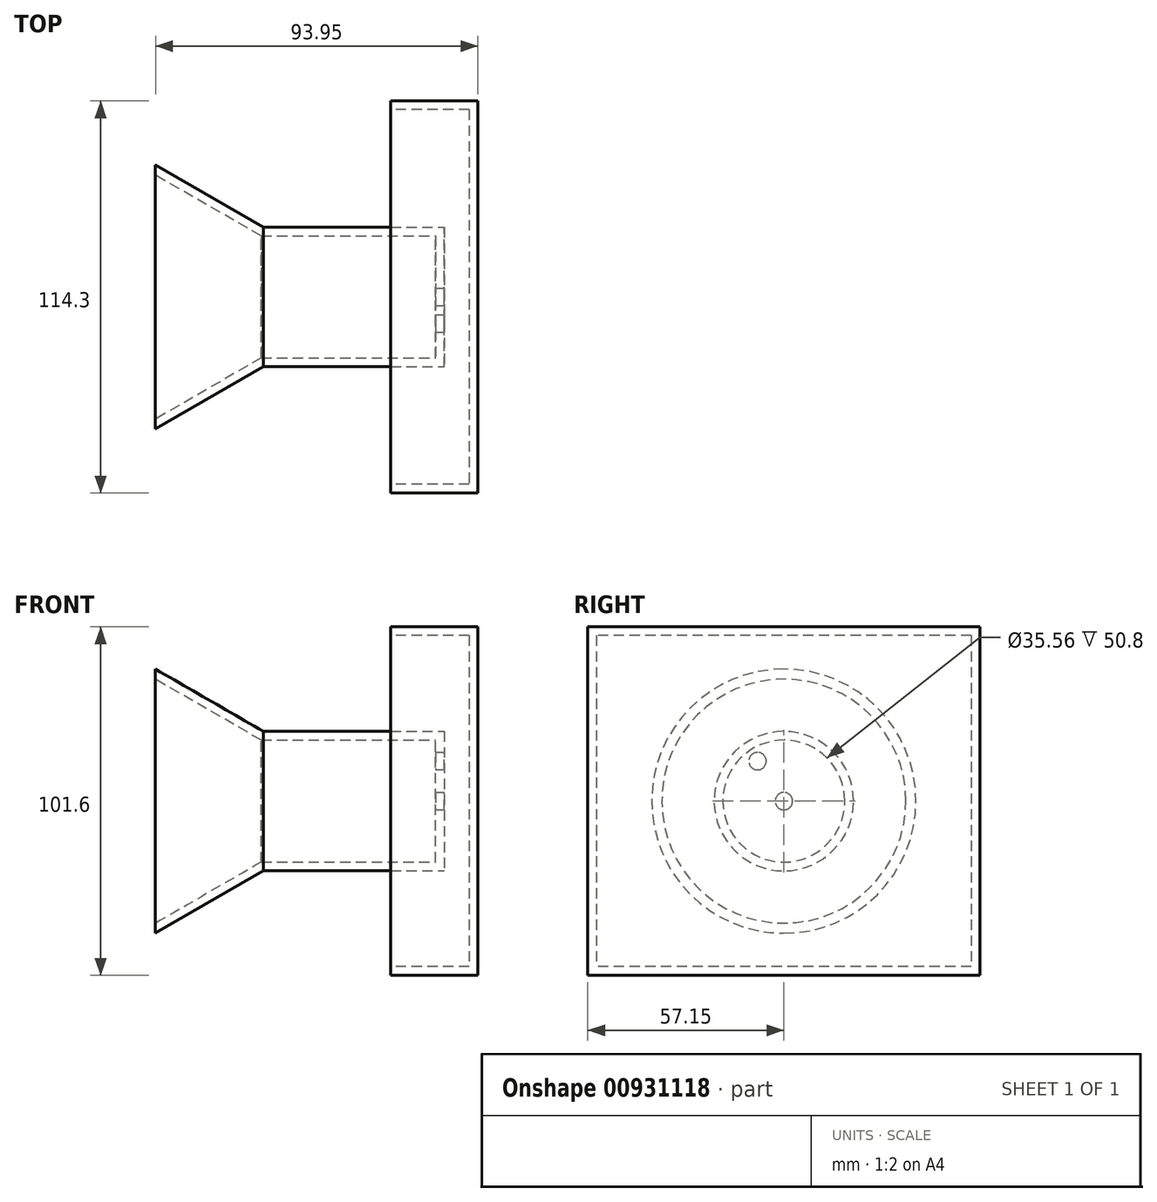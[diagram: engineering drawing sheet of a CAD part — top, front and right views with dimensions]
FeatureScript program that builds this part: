
annotation { "Feature Type Name" : "Feature", "Feature Type Description" : "" }
export const myFeature = defineFeature(function(context is Context, id is Id, definition is map)
    precondition{}
    {
        {
            var Q0;
            Q0=qCreatedBy(makeId("Front.planeOp"),FACE);
            var sketch = newSketch(context, id + "F0", { "sketchPlane" : qUnion([Q0])});
            skLineSegment(sketch, "E0", {"start": v(-55.85, 35.56) * mm, "end": v(-25.06, 17.78) * mm});
            skLineSegment(sketch, "E1", {"start": v(-25.06, 17.78) * mm, "end": v(25.74, 17.78) * mm});
            skLineSegment(sketch, "E2", {"start": v(25.74, 17.78) * mm, "end": v(25.74, 0) * mm});
            skLineSegment(sketch, "E3", {"start": v(25.74, 0) * mm, "end": v(-55.85, 0) * mm});
            skLineSegment(sketch, "E4", {"start": v(-55.85, 0) * mm, "end": v(-55.85, 35.56) * mm});
            skSolve(sketch);
        }
        {
            var Q0;
            Q0=makeQuery(id+"F0.imprint","IMPRINT",FACE,{"disambiguationData":[TD([[makeQuery(id+"F0.imprint","IMPRINT",EDGE,{"derivedFrom":sQuery(id+"F0.wireOp",EDGE,"E0")}),-1.0]])]});
            var Q1;
            Q1=sQuery(id+"F0.wireOp",EDGE,"E3");
            revolve(context, id + "F1", {"surfaceOperationType" : NewSurfaceOperationType.NEW, "entities" : qUnion([Q0]), "axis" : qUnion([Q1]), "revolveType" : RevolveType.FULL});
        }
        {
            var Q0;
            Q0=makeQuery(id+"F1.opRevolve","SWEPT_FACE",FACE,{"disambiguationData":[OSD([sQuery(id+"F0.wireOp",EDGE,"E4")])]});
            var Q1;
            Q1=makeQuery(id+"F1.opRevolve","SWEPT_BODY",BODY,{"disambiguationData":[OSD([sQuery(id+"F0.wireOp",EDGE,"E0"),sQuery(id+"F0.wireOp",EDGE,"E1"),sQuery(id+"F0.wireOp",EDGE,"E2"),sQuery(id+"F0.wireOp",EDGE,"E3"),sQuery(id+"F0.wireOp",EDGE,"E4")])]});
            shell(context, id + "F2", {"entities" : qUnion([Q0]), "parts" : qUnion([Q1]), "thickness" : 2.54 * mm, "oppositeDirection" : true});
        }
        {
            var Q0;
            Q0=makeQuery(id+"F1.opRevolve","SWEPT_FACE",FACE,{"disambiguationData":[OSD([sQuery(id+"F0.wireOp",EDGE,"E2")])]});
            var sketch = newSketch(context, id + "F3", { "sketchPlane" : qUnion([Q0])});
            skCircle(sketch, "E5", {"center": v(-7.67, 11.68) * mm, "radius": 2.54 * mm});
            skCircle(sketch, "E6", {"center": v(0, 0) * mm, "radius": 13.97 * mm, "construction": true});
            skSolve(sketch);
        }
        {
            var Q0;
            Q0 = qSketchRegion(id + "F3", true);
            extrude(context, id + "F4", {"entities" : qUnion([Q0]), "operationType" : NewBodyOperationType.REMOVE, "oppositeDirection" : true, "depth" : 25.4 * mm, "offsetDistance" : 25.4 * mm});
        }
        {
            var Q0;
            Q0=makeQuery(id+"F1.opRevolve","SWEPT_FACE",FACE,{"disambiguationData":[OSD([sQuery(id+"F0.wireOp",EDGE,"E2")])]});
            var sketch = newSketch(context, id + "F5", { "sketchPlane" : qUnion([Q0])});
            skCircle(sketch, "E7", {"center": v(0, 0) * mm, "radius": 2.54 * mm});
            skSolve(sketch);
        }
        {
            var Q0;
            Q0 = qSketchRegion(id + "F5", true);
            extrude(context, id + "F6", {"entities" : qUnion([Q0]), "operationType" : NewBodyOperationType.REMOVE, "oppositeDirection" : true, "depth" : 25.4 * mm, "offsetDistance" : 25.4 * mm});
        }
        {
            var Q0;
            Q0=qCreatedBy(makeId("Right.planeOp"),FACE);
            cPlane(context, id + "F7", {"entities" : qUnion([Q0]), "cplaneType" : CPlaneType.OFFSET, "offset" : 12.7 * mm, "width" : 152.4 * mm, "height" : 152.4 * mm});
        }
        {
            var Q0;
            Q0=qCreatedBy(id+"F7.planeOp",FACE);
            var sketch = newSketch(context, id + "F8", { "sketchPlane" : qUnion([Q0])});
            skLineSegment(sketch, "E8.bottom", {"start": v(57.15, 50.8) * mm, "end": v(-57.15, 50.8) * mm});
            skLineSegment(sketch, "E8.top", {"start": v(57.15, -50.8) * mm, "end": v(-57.15, -50.8) * mm});
            skLineSegment(sketch, "E8.left", {"start": v(57.15, 50.8) * mm, "end": v(57.15, -50.8) * mm});
            skLineSegment(sketch, "E8.right", {"start": v(-57.15, 50.8) * mm, "end": v(-57.15, -50.8) * mm});
            skPoint(sketch, "E8.middle", {"position": v(0, 0) * mm});
            skSolve(sketch);
        }
        {
            var Q0;
            Q0 = qSketchRegion(id + "F8", true);
            extrude(context, id + "F9", {"entities" : qUnion([Q0]), "depth" : 25.4 * mm, "offsetDistance" : 25.4 * mm});
        }
        {
            var Q0;
            Q0=makeQuery(id+"F9.opExtrude","CAP_FACE",FACE,{"disambiguationData":[OSD([sQuery(id+"F8.wireOp",EDGE,"E8.bottom"),sQuery(id+"F8.wireOp",EDGE,"E8.top"),sQuery(id+"F8.wireOp",EDGE,"E8.left"),sQuery(id+"F8.wireOp",EDGE,"E8.right")])],"isStart":true});
            shell(context, id + "F10", {"entities" : qUnion([Q0]), "thickness" : 2.54 * mm});
        }
    });
